# Revit family: Drain_Trench_Elevator-Zurn-Z899-EL
name_source: partatom
category: Plumbing Fixtures
units: mm (PartAtom-declared; Revit-internal decimal feet)

## family parameters
Always vertical = Yes
Cut with Voids When Loaded = No
Maintain Annotation Orientation = No
OmniClass Number = 23.70.50.21.24.14
OmniClass Title = Deck Waste Water Drains
Part Type = Normal
Room Calculation Point = No
Round Connector Dimension = Use Radius
Shared = No
Work Plane-Based = No

## types (30) — shared parameters
Actual Outlet Radius = 0' - 2 1/4"
Assembly Code = D2030300
CW Connection = Yes
Channel Depth = 0' - 2 1/2"
Default Elevation = 2' - 0"
Description = FSAE/OEE Trench Drainage System
HW Connection = No
Main Material = Steel - Zurn - Stainless - Type 304
Manufacturer = Zurn Water, LLC
Manufacurer Brand = Zurn
Model = Z899-EL
Modified Date = January 6, 2025
Nominal Outlet Radius = 0' - 2"
Outlet Depth = 0' - 6"
Outlet Radius = 0' - 2"
Product Documentation Link = https://files.zurn.com
Product Installation Sheet = https://files.zurn.com
Product Page URL = https://www.zurn.com
Trap Primer Radius = 0' - 0 1/4"
URL = www.zurn.com
Vent Connection = No
WFU = 1
Waste Connection = Yes
zero-valued in all types: CWFU, HWFU

## per-type parameters (varying)
| type | Anchor Straps-36 | Anchor Straps-48 | Anchor Straps-60 | Anchor Straps-72 | Anchor Straps-96 | Length_A | Outlet Location (Centered) | Product data url | Type Comments | Width_C |
| 12 Wide x 96 Long Channel (Less Straps) | No | No | No | No | No | 8' - 0" | 4' - 0" | https://bimobject.com | Z899-EL-12 x 96 (Less Straps) w/ Trap Primer Option | 1' - 0" |
| 12 Wide x 96 Long Channel | Yes | Yes | Yes | Yes | Yes | 8' - 0" | 4' - 0" | https://bimobject.com | Z899-EL-12 x 96 w/ Trap Primer Option | 1' - 0" |
| 12 Wide x 72 Long Channel | Yes | Yes | Yes | Yes | No | 6' - 0" | 3' - 0" | https://bimobject.com | Z899-EL-12 x 72 w/ Trap Primer Option | 1' - 0" |
| 12 Wide x 72 Long Channel (Less Straps) | No | No | No | No | No | 6' - 0" | 3' - 0" | https://bimobject.com | Z899-EL-12 x 72 (Less Straps) w/ Trap Primer Option | 1' - 0" |
| 12 Wide x 60 Long Channel (Less Straps) | No | No | No | No | No | 5' - 0" | 2' - 6" | https://bimobject.com | Z899-EL-12 x 60 (Less Straps) w/ Trap Primer Option | 1' - 0" |
| 12 Wide x 60 Long Channel | Yes | Yes | Yes | No | No | 5' - 0" | 2' - 6" | https://bimobject.com | Z899-EL-12 x 60 w/ Trap Primer Option | 1' - 0" |
| 12 Wide x 48 Long Channel | Yes | Yes | No | No | No | 4' - 0" | 2' - 0" | https://bimobject.com | Z899-EL-12 x 48 w/ Trap Primer Option | 1' - 0" |
| 12 Wide x 48 Long Channel (Less Straps) | No | No | No | No | No | 4' - 0" | 2' - 0" | https://bimobject.com | Z899-EL-12 x 48 (Less Straps) w/ Trap Primer Option | 1' - 0" |
| 12 Wide x 36 Long Channel (Less Straps) | No | No | No | No | No | 3' - 0" | 1' - 6" | https://bimobject.com | Z899-EL-12 x 36 (Less Straps) w/ Trap Primer Option | 1' - 0" |
| 12 Wide x 36 Long Channel | Yes | No | No | No | No | 3' - 0" | 1' - 6" | https://bimobject.com | Z899-EL-12 x 36 w/ Trap Primer Option | 1' - 0" |
| 10 Wide x 36 Long Channel | Yes | No | No | No | No | 3' - 0" | 1' - 6" | https://bimobject.com | Z899-EL-10 x 36 w/ Trap Primer Option | 0' - 10" |
| 8 Wide x 36 Long Channel | Yes | No | No | No | No | 3' - 0" | 1' - 6" | https://bimobject.com | Z899-EL-8 x 36 w/ Trap Primer Option | 0' - 8" |
| 10 Wide x 36 Long Channel (Less Straps) | No | No | No | No | No | 3' - 0" | 1' - 6" | https://bimobject.com | Z899-EL-10 x 36 (Less Straps) w/ Trap Primer Option | 0' - 10" |
| 8 Wide x 36 Long Channel (Less Straps) | No | No | No | No | No | 3' - 0" | 1' - 6" | https://bimobject.com | Z899-EL-8 x 36 (Less Straps) w/ Trap Primer Option | 0' - 8" |
| 10 Wide x 48 Long Channel | Yes | Yes | No | No | No | 4' - 0" | 2' - 0" | https://bimobject.com | Z899-EL-10 x 48 w/ Trap Primer Option | 0' - 10" |
| 10 Wide x 48 Long Channel (Less Straps) | No | No | No | No | No | 4' - 0" | 2' - 0" |  | Z899-EL-10 x 48 (Less Straps) w/ Trap Primer Option | 0' - 10" |
| 8 Wide x 48 Long Channel | Yes | Yes | No | No | No | 4' - 0" | 2' - 0" | https://bimobject.com | Z899-EL-8 x 48 w/ Trap Primer Option | 0' - 8" |
| 8 Wide x 48 Long Channel (Less Straps) | No | No | No | No | No | 4' - 0" | 2' - 0" | https://bimobject.com | Z899-EL-8 x 48 (Less Straps) w/ Trap Primer Option | 0' - 8" |
| 10 Wide x 60 Long Channel | Yes | Yes | Yes | No | No | 5' - 0" | 2' - 6" | https://bimobject.com | Z899-EL-10 x 60 w/ Trap Primer Option | 0' - 10" |
| 10 Wide x 60 Long Channel (Less Straps) | No | No | No | No | No | 5' - 0" | 2' - 6" |  | Z899-EL-10 x 60 (Less Straps) w/ Trap Primer Option | 0' - 10" |
| 8 Wide x 60 Long Channel | Yes | Yes | Yes | No | No | 5' - 0" | 2' - 6" | https://bimobject.com | Z899-EL-8 x 60 w/ Trap Primer Option | 0' - 8" |
| 8 Wide x 60 Long Channel (Less Straps) | No | No | No | No | No | 5' - 0" | 2' - 6" | https://bimobject.com | Z899-EL-8 x 60 (Less Straps) w/ Trap Primer Option | 0' - 8" |
| 10 Wide x 72 Long Channel | Yes | Yes | Yes | Yes | No | 6' - 0" | 3' - 0" | https://bimobject.com | Z899-EL-10 x 72 w/ Trap Primer Option | 0' - 10" |
| 10 Wide x 72 Long Channel (Less Straps) | No | No | No | No | No | 6' - 0" | 3' - 0" |  | Z899-EL-10 x 72 (Less Straps) w/ Trap Primer Option | 0' - 10" |
| 8 Wide x 72 Long Channel | Yes | Yes | Yes | Yes | No | 6' - 0" | 3' - 0" | https://bimobject.com | Z899-EL-8 x 72 w/ Trap Primer Option | 0' - 8" |
| 8 Wide x 72 Long Channel (Less Straps) | No | No | No | No | No | 6' - 0" | 3' - 0" | https://bimobject.com | Z899-EL-8 x 72 (Less Straps) w/ Trap Primer Option | 0' - 8" |
| 10 Wide x 96 Long Channel | Yes | Yes | Yes | Yes | Yes | 8' - 0" | 4' - 0" | https://bimobject.com | Z899-EL-10 x 96 w/ Trap Primer Option | 0' - 10" |
| 10 Wide x 96 Long Channel (Less Straps) | No | No | No | No | No | 8' - 0" | 4' - 0" | https://bimobject.com | Z899-EL-10 x 96 (Less Straps) w/ Trap Primer Option | 0' - 10" |
| 8 Wide x 96 Long Channel | Yes | Yes | Yes | Yes | Yes | 8' - 0" | 4' - 0" | https://bimobject.com | Z899-EL-8 x 96 w/ Trap Primer Option | 0' - 8" |
| 8 Wide x 96 Long Channel (Less Straps) | No | No | No | No | No | 8' - 0" | 4' - 0" | Z899-EL-8 x 72 w/ Trap Primer Option | Z899-EL-8 x 96 (Less Straps) w/ Trap Primer Option | 0' - 8" |

## geometry (parser evidence)
native form markers: Sweep x2
no freeform markers — native parametric forms only
